# Revit family: P191568KX-074c_KOSE900H
name_source: partatom
category: Specialty Equipment
units: mm (PartAtom-declared; Revit-internal decimal feet)

## family parameters
Always vertical = Yes
Cut with Voids When Loaded = No
Enable Cutting in Views = No
Maintain Annotation Orientation = No
Part Type = Normal
Room Calculation Point = No
Round Connector Dimension = Use Diameter
Shared = No
Work Plane-Based = No

## types (1)
- KOSE900HSS
    Apparent Load = 0 VA
    Body Material = ARCAT - Metal - Steel - Stainless
    Clearance Material = ARCAT - Clearance
    Default Elevation = 0"
    Depth = 27 1/8"
    Description = Smart Oven+ 30" Single Oven with Powered Attachments
Four intelligent+ simple avec accessoires optimisés et fini PrintShield™, 30 po
    Display Panel Material = ARCAT - Glass - Black
    Door Material = ARCAT - Metal - Steel - Stainless
    Family Name = COOKING
    Feature 1 = Smart Oven+ Powered Attachments
Four intelligent + accessoires optimisés
    Feature 2 = Smart Oven+ Mobile App Connectivity
Connectivité à l’application mobile du four intelligent+
    Feature 3 = +Grill Attachment
+Gril
    Glass Material = ARCAT - Glass - Tempered - Black
    Handle Material = ARCAT - Metal - Steel - Gray
    Height = 28 3/4"
    Installation-Fabrication = https://www.whirlpool.com
https://www.whirlpool.com
    Manufacturer = Kitchen Aid
    Model = KOSE900HSS
    Voltage = 0 V
    Width = 30"

## geometry (parser evidence)
native form markers: Sweep x6
no freeform markers — native parametric forms only
